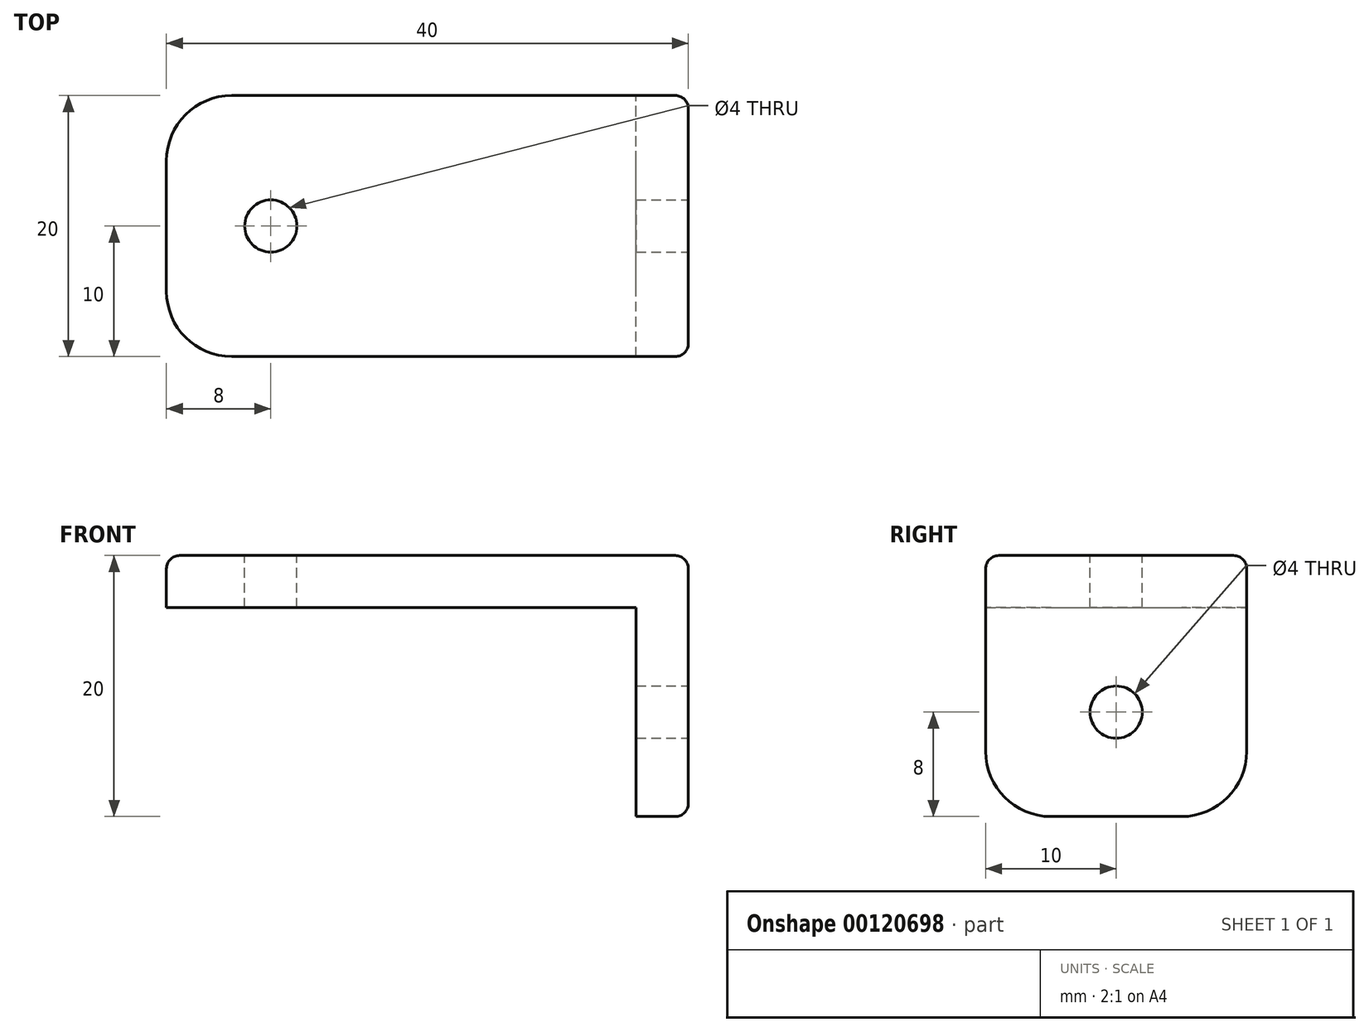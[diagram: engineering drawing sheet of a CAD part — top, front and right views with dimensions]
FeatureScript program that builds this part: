
annotation { "Feature Type Name" : "Feature", "Feature Type Description" : "" }
export const myFeature = defineFeature(function(context is Context, id is Id, definition is map)
    precondition{}
    {
        {
            var Q0;
            Q0=qCreatedBy(makeId("Front.planeOp"),FACE);
            var sketch = newSketch(context, id + "F0", { "sketchPlane" : qUnion([Q0])});
            skLineSegment(sketch, "E0", {"start": v(0, 0) * mm, "end": v(0, 20) * mm});
            skLineSegment(sketch, "E1", {"start": v(0, 20) * mm, "end": v(-40, 20) * mm});
            skLineSegment(sketch, "E2", {"start": v(-40, 20) * mm, "end": v(-40, 16) * mm});
            skLineSegment(sketch, "E3", {"start": v(-40, 16) * mm, "end": v(-4, 16) * mm});
            skLineSegment(sketch, "E4", {"start": v(-4, 16) * mm, "end": v(-4, 0) * mm});
            skLineSegment(sketch, "E5", {"start": v(-4, 0) * mm, "end": v(0, 0) * mm});
            skSolve(sketch);
        }
        {
            var Q0;
            Q0 = qSketchRegion(id + "F0", true);
            extrude(context, id + "F1", {"entities" : qUnion([Q0]), "depth" : 20 * mm});
        }
        {
            var Q0;
            Q0=makeQuery(id+"F1.opExtrude","SWEPT_FACE",FACE,{"disambiguationData":[OSD([sQuery(id+"F0.wireOp",EDGE,"E1")])]});
            var sketch = newSketch(context, id + "F2", { "sketchPlane" : qUnion([Q0])});
            skCircle(sketch, "E6", {"center": v(-32, -10) * mm, "radius": 2 * mm});
            skPoint(sketch, "E6.centerSnap0", {"position": v(-40, -10) * mm});
            skSolve(sketch);
        }
        {
            var Q0;
            Q0 = qSketchRegion(id + "F2", true);
            extrude(context, id + "F3", {"entities" : qUnion([Q0]), "operationType" : NewBodyOperationType.REMOVE, "oppositeDirection" : true, "depth" : 25 * mm});
        }
        {
            var Q0;
            Q0=makeQuery(id+"F1.opExtrude","SWEPT_FACE",FACE,{"disambiguationData":[OSD([sQuery(id+"F0.wireOp",EDGE,"E0")])]});
            var sketch = newSketch(context, id + "F4", { "sketchPlane" : qUnion([Q0])});
            skCircle(sketch, "E7", {"center": v(-10, 8) * mm, "radius": 2 * mm});
            skPoint(sketch, "E7.centerSnap0", {"position": v(-10, 0) * mm});
            skSolve(sketch);
        }
        {
            var Q0;
            Q0 = qSketchRegion(id + "F4", true);
            extrude(context, id + "F5", {"entities" : qUnion([Q0]), "operationType" : NewBodyOperationType.REMOVE, "oppositeDirection" : true, "depth" : 25 * mm});
        }
        {
            var Q0;
            Q0=makeQuery(id+"F1.opExtrude","CAP_EDGE",EDGE,{"disambiguationData":[OSD([sQuery(id+"F0.wireOp",EDGE,"E5")])],"isStart":false});
            var Q1;
            Q1=makeQuery(id+"F1.opExtrude","CAP_EDGE",EDGE,{"disambiguationData":[OSD([sQuery(id+"F0.wireOp",EDGE,"E5")])],"isStart":true});
            var Q2;
            Q2=makeQuery(id+"F1.opExtrude","CAP_EDGE",EDGE,{"disambiguationData":[OSD([sQuery(id+"F0.wireOp",EDGE,"E2")])],"isStart":false});
            var Q3;
            Q3=makeQuery(id+"F1.opExtrude","CAP_EDGE",EDGE,{"disambiguationData":[OSD([sQuery(id+"F0.wireOp",EDGE,"E2")])],"isStart":true});
            fillet(context, id + "F6", {"entities" : qUnion([Q0, Q1, Q2, Q3]), "radius" : 5 * mm, "tangentPropagation" : true, "allowEdgeOverflow" : false});
        }
        {
            var Q0;
            Q0=makeQuery(id+"F1.opExtrude","CAP_EDGE",EDGE,{"disambiguationData":[OSD([sQuery(id+"F0.wireOp",EDGE,"E1")])],"isStart":false});
            var Q1;
            Q1=makeQuery(id+"F1.opExtrude","CAP_EDGE",EDGE,{"disambiguationData":[OSD([sQuery(id+"F0.wireOp",EDGE,"E0")])],"isStart":false});
            var Q2;
            Q2=makeQuery(id+"F1.opExtrude","SWEPT_EDGE",EDGE,{"disambiguationData":[OSD([sQuery(id+"F0.wireOp",EDGE,"E0"),sQuery(id+"F0.wireOp",EDGE,"E1")])]});
            fillet(context, id + "F7", {"entities" : qUnion([Q0, Q1, Q2]), "radius" : 1 * mm, "tangentPropagation" : true, "allowEdgeOverflow" : false});
        }
    });
